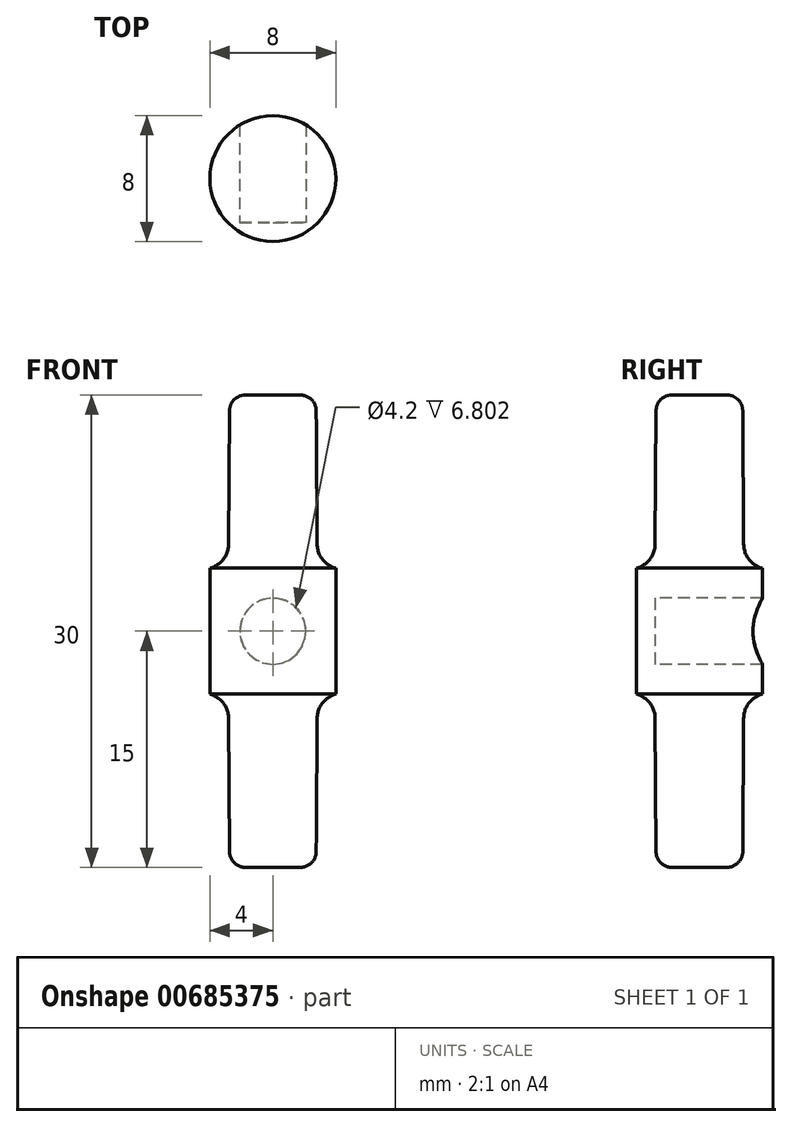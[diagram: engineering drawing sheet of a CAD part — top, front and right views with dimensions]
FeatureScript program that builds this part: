
annotation { "Feature Type Name" : "Feature", "Feature Type Description" : "" }
export const myFeature = defineFeature(function(context is Context, id is Id, definition is map)
    precondition{}
    {
        {
            var Q0;
            Q0=qCreatedBy(makeId("Top.planeOp"),FACE);
            var sketch = newSketch(context, id + "F0", { "sketchPlane" : qUnion([Q0])});
            skCircle(sketch, "E0", {"center": v(0, 0) * mm, "radius": 2.85 * mm});
            skCircle(sketch, "E1", {"center": v(0, 0) * mm, "radius": 4 * mm});
            skSolve(sketch);
        }
        {
            var Q0;
            Q0=makeQuery(id+"F0.imprint","IMPRINT",FACE,{"disambiguationData":[TD([[makeQuery(id+"F0.imprint","IMPRINT",EDGE,{"derivedFrom":sQuery(id+"F0.wireOp",EDGE,"E0")}),1.0]])]});
            extrude(context, id + "F1", {"entities" : qUnion([Q0]), "depth" : 15 * mm, "offsetDistance" : 25 * mm, "hasDraft" : true, "draftAngle" : 0.4 * degree, "draftPullDirection" : true});
        }
        {
            var Q0;
            Q0=makeQuery(id+"F0.imprint","IMPRINT",FACE,{"disambiguationData":[TD([[makeQuery(id+"F0.imprint","IMPRINT",EDGE,{"derivedFrom":sQuery(id+"F0.wireOp",EDGE,"E0")}),1.0]])]});
            extrude(context, id + "F2", {"entities" : qUnion([Q0]), "operationType" : NewBodyOperationType.ADD, "oppositeDirection" : true, "depth" : 15 * mm, "offsetDistance" : 25 * mm, "hasDraft" : true, "draftAngle" : .4 * degree, "draftPullDirection" : true});
        }
        {
            var Q0;
            Q0=makeQuery(id+"F0.imprint","IMPRINT",FACE,{"disambiguationData":[TD([[makeQuery(id+"F0.imprint","IMPRINT",EDGE,{"derivedFrom":sQuery(id+"F0.wireOp",EDGE,"E0")}),-1.0]])]});
            var Q1;
            Q1=makeQuery(id+"F0.imprint","IMPRINT",FACE,{"disambiguationData":[TD([[makeQuery(id+"F0.imprint","IMPRINT",EDGE,{"derivedFrom":sQuery(id+"F0.wireOp",EDGE,"E0")}),1.0]])]});
            extrude(context, id + "F3", {"entities" : qUnion([Q0, Q1]), "operationType" : NewBodyOperationType.ADD, "depth" : 4 * mm, "offsetDistance" : 25 * mm});
        }
        {
            var Q0;
            Q0=makeQuery(id+"F0.imprint","IMPRINT",FACE,{"disambiguationData":[TD([[makeQuery(id+"F0.imprint","IMPRINT",EDGE,{"derivedFrom":sQuery(id+"F0.wireOp",EDGE,"E0")}),-1.0]])]});
            var Q1;
            Q1=makeQuery(id+"F0.imprint","IMPRINT",FACE,{"disambiguationData":[TD([[makeQuery(id+"F0.imprint","IMPRINT",EDGE,{"derivedFrom":sQuery(id+"F0.wireOp",EDGE,"E0")}),1.0]])]});
            extrude(context, id + "F4", {"entities" : qUnion([Q0, Q1]), "operationType" : NewBodyOperationType.ADD, "oppositeDirection" : true, "depth" : 4 * mm, "offsetDistance" : 25 * mm});
        }
        {
            var Q0;
            Q0=makeQuery(id+"F1.opExtrude","CAP_EDGE",EDGE,{"disambiguationData":[OSD([sQuery(id+"F0.wireOp",EDGE,"E0")])],"isStart":false});
            var Q1;
            Q1=makeQuery(id+"F2.opExtrude","CAP_EDGE",EDGE,{"disambiguationData":[OSD([sQuery(id+"F0.wireOp",EDGE,"E0")])],"isStart":false});
            fillet(context, id + "F5", {"entities" : qUnion([Q0, Q1]), "radius" : 1 * mm, "tangentPropagation" : true, "allowEdgeOverflow" : false});
        }
        {
            var Q0;
            Q0=qCreatedBy(makeId("Front.planeOp"),FACE);
            var sketch = newSketch(context, id + "F6", { "sketchPlane" : qUnion([Q0])});
            skCircle(sketch, "E2", {"center": v(0, 0) * mm, "radius": 2.1 * mm});
            skSolve(sketch);
        }
        {
            var Q0;
            Q0=makeQuery(id+"F6.imprint","IMPRINT",FACE,{"disambiguationData":[TD([[makeQuery(id+"F6.imprint","IMPRINT",EDGE,{"derivedFrom":sQuery(id+"F6.wireOp",EDGE,"E2")}),1.0]])]});
            extrude(context, id + "F7", {"entities" : qUnion([Q0]), "operationType" : NewBodyOperationType.REMOVE, "oppositeDirection" : true, "depth" : 4.2 * mm, "offsetDistance" : 25 * mm});
        }
        {
            var Q0;
            Q0=makeQuery(id+"F6.imprint","IMPRINT",FACE,{"disambiguationData":[TD([[makeQuery(id+"F6.imprint","IMPRINT",EDGE,{"derivedFrom":sQuery(id+"F6.wireOp",EDGE,"E2")}),1.0]])]});
            extrude(context, id + "F8", {"entities" : qUnion([Q0]), "operationType" : NewBodyOperationType.REMOVE, "depth" : 2.8 * mm, "offsetDistance" : 25 * mm});
        }
        {
            var Q0;
            Q0=makeQuery(id+"F4.boolean.opBoolean","INTERSECT",EDGE,{"derivedFrom":[makeQuery(id+"F2.opExtrude","SWEPT_FACE",FACE,{"disambiguationData":[OSD([sQuery(id+"F0.wireOp",EDGE,"E0")])]}),makeQuery(id+"F4.opExtrude","CAP_FACE",FACE,{"disambiguationData":[OSD([sQuery(id+"F0.wireOp",EDGE,"E1")])],"isStart":false})]});
            var Q1;
            Q1=makeQuery(id+"F3.boolean.opBoolean","INTERSECT",EDGE,{"derivedFrom":[makeQuery(id+"F1.opExtrude","SWEPT_FACE",FACE,{"disambiguationData":[OSD([sQuery(id+"F0.wireOp",EDGE,"E0")])]}),makeQuery(id+"F3.opExtrude","CAP_FACE",FACE,{"disambiguationData":[OSD([sQuery(id+"F0.wireOp",EDGE,"E1")])],"isStart":false})]});
            fillet(context, id + "F9", {"entities" : qUnion([Q0, Q1]), "radius" : 1.6 * mm, "tangentPropagation" : true, "allowEdgeOverflow" : false});
        }
    });
